# Revit family: Table-Height_Adjustable-Teknion-BH_CB_Cross_Grain_Height_Adjustable_Rectangular_Worksurface_Mid_Height-R2018
name_source: partatom
category: Furniture
revit_build: Autodesk Revit 2018 (Build: 20190510_1515(x64)
units: mm (PartAtom-declared; Revit-internal decimal feet)

## family parameters
Always vertical = Yes
Cut with Voids When Loaded = No
OmniClass Number = 23.40.20.00
OmniClass Title = General Furniture and Specialties
Room Calculation Point = No
Shared = Yes
Work Plane-Based = No

## types (6) — shared parameters
Assembly Code = E2020200
Manufacturer = Teknion
Manufacturer Fax = 416.661.4586
Part Number = BH_CB
Product Documentation Link = https://www.teknion.com
Product Line = Expansion Casegoods
Product Page URL = https://www.teknion.com
Series = Expansion Casegoods
Sustainability Data = https://www.teknion.com
URL = www.teknion.com
Unit Weight URL = http://www.teknion.com
Warranty = http://www.teknion.com

## per-type parameters (varying)
| type | Depth | Description | Model | Worksurface Thickness |
| 1 3/16" Worksurface Thickness, 27" Depth | 27 " | Cross Grain Height-Adjustable Rectangular Worksurface - Mid-Height, 1 3/16" Worksurface Thickness, Mid-Height Configuration, 27" Depth | BHMCBK27_ | 1.189 " |
| 1 3/16" Worksurface Thickness, 24" Depth | 24 " | Cross Grain Height-Adjustable Rectangular Worksurface - Mid-Height, 1 3/16" Worksurface Thickness, Mid-Height Configuration, 24" Depth | BHMCBK24_ | 1.189 " |
| 1 3/16" Worksurface Thickness, 21" Depth | 21 " | Cross Grain Height-Adjustable Rectangular Worksurface - Mid-Height, 1 3/16" Worksurface Thickness, Mid-Height Configuration, 21" Depth | BHMCBK21_ | 1.189 " |
| 1 9/16" Worksurface Thickness, 24" Depth | 24 " | Cross Grain Height-Adjustable Rectangular Worksurface - Mid-Height, 1 9/16" Worksurface Thickness, Mid-Height Configuration, 24" Depth | BHXCBK24_ | 1.555 " |
| 1 9/16" Worksurface Thickness, 21" Depth | 21 " | Cross Grain Height-Adjustable Rectangular Worksurface - Mid-Height, 1 9/16" Worksurface Thickness, Mid-Height Configuration, 21" Depth | BHXCBK21_ | 1.555 " |
| 1 9/16" Worksurface Thickness, 27" Depth | 27 " | Cross Grain Height-Adjustable Rectangular Worksurface - Mid-Height, 1 9/16" Worksurface Thickness, Mid-Height Configuration, 27" Depth | BHXCBK27_ | 1.555 " |

## geometry (parser evidence)
native form markers: Sweep x4
no freeform markers — native parametric forms only
